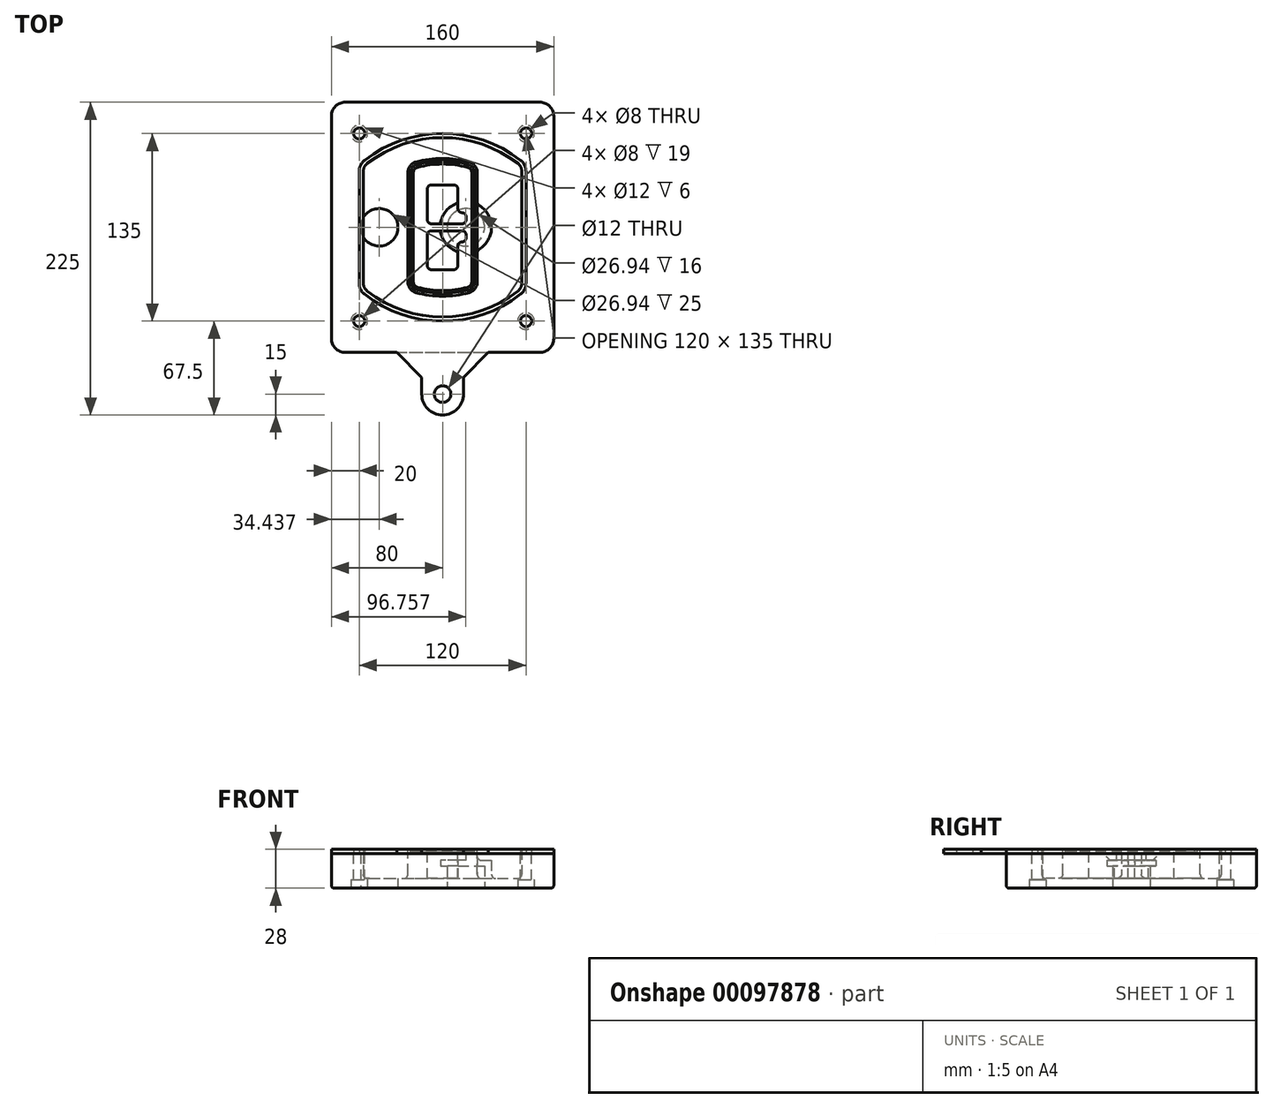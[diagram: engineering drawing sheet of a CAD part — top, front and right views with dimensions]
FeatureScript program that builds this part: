
annotation { "Feature Type Name" : "Feature", "Feature Type Description" : "" }
export const myFeature = defineFeature(function(context is Context, id is Id, definition is map)
    precondition{}
    {
        {
            var Q0;
            Q0=qCreatedBy(makeId("Top.planeOp"),FACE);
            var sketch = newSketch(context, id + "F0", { "sketchPlane" : qUnion([Q0])});
            skPoint(sketch, "E0.rect.middle", {"position": v(0, 0) * mm});
            skLineSegment(sketch, "E1.bottom", {"start": v(-70, -90) * mm, "end": v(70, -90) * mm});
            skLineSegment(sketch, "E1.top", {"start": v(-70, 90) * mm, "end": v(70, 90) * mm});
            skLineSegment(sketch, "E1.left", {"start": v(-80, -80) * mm, "end": v(-80, 80) * mm});
            skLineSegment(sketch, "E1.right", {"start": v(80, -80) * mm, "end": v(80, 80) * mm});
            skLineSegment(sketch, "E2", {"start": v(-80, 90) * mm, "end": v(80, -90) * mm, "construction": true});
            skLineSegment(sketch, "E3", {"start": v(80, 90) * mm, "end": v(-80, -90) * mm, "construction": true});
            skCircle(sketch, "E4", {"center": v(-60, 67.5) * mm, "radius": 4 * mm});
            skCircle(sketch, "E5", {"center": v(60, 67.5) * mm, "radius": 4 * mm});
            skCircle(sketch, "E6", {"center": v(60, -67.5) * mm, "radius": 4 * mm});
            skCircle(sketch, "E7", {"center": v(-60, -67.5) * mm, "radius": 4 * mm});
            skLineSegment(sketch, "E8", {"start": v(-60, 67.5) * mm, "end": v(60, 67.5) * mm, "construction": true});
            skLineSegment(sketch, "E9", {"start": v(60, 67.5) * mm, "end": v(60, -67.5) * mm, "construction": true});
            skLineSegment(sketch, "E10", {"start": v(60, -67.5) * mm, "end": v(-60, -67.5) * mm, "construction": true});
            skLineSegment(sketch, "E11", {"start": v(-60, -67.5) * mm, "end": v(-60, 67.5) * mm, "construction": true});
            skLineSegment(sketch, "E12", {"start": v(-60, 40.3) * mm, "end": v(-60, -40.3) * mm});
            skLineSegment(sketch, "E13", {"start": v(60, 40.3) * mm, "end": v(60, -40.3) * mm});
            skArc(sketch, "E14", {"start": v(56.15, 48.18) * mm, "mid": v(0, 67.5) * mm, "end": v(-56.15, 48.18) * mm});
            skArc(sketch, "E15", {"start": v(-56.15, -48.18) * mm, "mid": v(0, -67.5) * mm, "end": v(56.15, -48.18) * mm});
            skLineSegment(sketch, "E16", {"start": v(-60, 0) * mm, "end": v(60, 0) * mm, "construction": true});
            skPoint(sketch, "E17.visualSharp", {"position": v(-60, -45) * mm});
            skArc(sketch, "E17.filletArc", {"start": v(-60, -40.3) * mm, "mid": v(-58.99, -44.68) * mm, "end": v(-56.15, -48.18) * mm});
            skPoint(sketch, "E18.visualSharp", {"position": v(-60, 45) * mm});
            skArc(sketch, "E18.filletArc", {"start": v(-56.15, 48.18) * mm, "mid": v(-58.99, 44.68) * mm, "end": v(-60, 40.3) * mm});
            skPoint(sketch, "E19.visualSharp", {"position": v(60, 45) * mm});
            skArc(sketch, "E19.filletArc", {"start": v(60, 40.3) * mm, "mid": v(58.99, 44.68) * mm, "end": v(56.15, 48.18) * mm});
            skPoint(sketch, "E20.visualSharp", {"position": v(60, -45) * mm});
            skArc(sketch, "E20.filletArc", {"start": v(56.15, -48.18) * mm, "mid": v(58.99, -44.68) * mm, "end": v(60, -40.3) * mm});
            skPoint(sketch, "E21.visualSharp", {"position": v(-80, 90) * mm});
            skArc(sketch, "E21.filletArc", {"start": v(-70, 90) * mm, "mid": v(-77.07, 87.07) * mm, "end": v(-80, 80) * mm});
            skPoint(sketch, "E22.visualSharp", {"position": v(80, 90) * mm});
            skArc(sketch, "E22.filletArc", {"start": v(80, 80) * mm, "mid": v(77.07, 87.07) * mm, "end": v(70, 90) * mm});
            skPoint(sketch, "E23.visualSharp", {"position": v(80, -90) * mm});
            skArc(sketch, "E23.filletArc", {"start": v(70, -90) * mm, "mid": v(77.07, -87.07) * mm, "end": v(80, -80) * mm});
            skPoint(sketch, "E24.visualSharp", {"position": v(-80, -90) * mm});
            skArc(sketch, "E24.filletArc", {"start": v(-80, -80) * mm, "mid": v(-77.07, -87.07) * mm, "end": v(-70, -90) * mm});
            skArc(sketch, "E25.0", {"start": v(57, 40.3) * mm, "mid": v(56.3, 43.36) * mm, "end": v(54.3, 45.81) * mm});
            skLineSegment(sketch, "E25.1", {"start": v(57, 40.3) * mm, "end": v(57, -40.3) * mm});
            skArc(sketch, "E25.2", {"start": v(54.3, -45.81) * mm, "mid": v(56.3, -43.36) * mm, "end": v(57, -40.3) * mm});
            skArc(sketch, "E25.3", {"start": v(-54.3, -45.81) * mm, "mid": v(0, -64.5) * mm, "end": v(54.3, -45.81) * mm});
            skArc(sketch, "E25.4", {"start": v(-57, -40.3) * mm, "mid": v(-56.3, -43.36) * mm, "end": v(-54.3, -45.81) * mm});
            skArc(sketch, "E25.5", {"start": v(54.3, 45.81) * mm, "mid": v(0, 64.5) * mm, "end": v(-54.3, 45.81) * mm});
            skLineSegment(sketch, "E25.6", {"start": v(-57, 40.3) * mm, "end": v(-57, -40.3) * mm});
            skArc(sketch, "E25.7", {"start": v(-54.3, 45.81) * mm, "mid": v(-56.3, 43.36) * mm, "end": v(-57, 40.3) * mm});
            skArc(sketch, "E26.0", {"start": v(-58.62, 51.33) * mm, "mid": v(-62.58, 46.43) * mm, "end": v(-64, 40.3) * mm});
            skArc(sketch, "E26.1", {"start": v(58.62, 51.33) * mm, "mid": v(0, 71.5) * mm, "end": v(-58.62, 51.33) * mm});
            skArc(sketch, "E26.2", {"start": v(64, 40.3) * mm, "mid": v(62.58, 46.43) * mm, "end": v(58.62, 51.33) * mm});
            skLineSegment(sketch, "E26.3", {"start": v(64, 40.3) * mm, "end": v(64, -40.3) * mm});
            skArc(sketch, "E26.4", {"start": v(58.62, -51.33) * mm, "mid": v(62.58, -46.43) * mm, "end": v(64, -40.3) * mm});
            skLineSegment(sketch, "E26.5", {"start": v(-64, 40.3) * mm, "end": v(-64, -40.3) * mm});
            skArc(sketch, "E26.6", {"start": v(-58.62, -51.33) * mm, "mid": v(0, -71.5) * mm, "end": v(58.62, -51.33) * mm});
            skArc(sketch, "E26.7", {"start": v(-64, -40.3) * mm, "mid": v(-62.58, -46.43) * mm, "end": v(-58.62, -51.33) * mm});
            skSolve(sketch);
        }
        {
            var Q0;
            Q0=makeQuery(id+"F0.imprint","IMPRINT",FACE,{"disambiguationData":[TD([[makeQuery(id+"F0.imprint","IMPRINT",EDGE,{"derivedFrom":sQuery(id+"F0.wireOp",EDGE,"E1.bottom")}),1.0]])]});
            var Q1;
            Q1=makeQuery(id+"F0.imprint","IMPRINT",FACE,{"disambiguationData":[TD([[makeQuery(id+"F0.imprint","IMPRINT",EDGE,{"derivedFrom":sQuery(id+"F0.wireOp",EDGE,"E12")}),1.0]])]});
            var Q2;
            Q2=makeQuery(id+"F0.imprint","IMPRINT",FACE,{"disambiguationData":[TD([[makeQuery(id+"F0.imprint","IMPRINT",EDGE,{"derivedFrom":sQuery(id+"F0.wireOp",EDGE,"E25.0")}),1.0]])]});
            var Q3;
            Q3=makeQuery(id+"F0.imprint","IMPRINT",FACE,{"disambiguationData":[TD([[makeQuery(id+"F0.imprint","IMPRINT",EDGE,{"derivedFrom":sQuery(id+"F0.wireOp",EDGE,"E12")}),-1.0]])]});
            extrude(context, id + "F1", {"entities" : qUnion([Q0, Q1, Q2, Q3]), "oppositeDirection" : true, "depth" : 25 * mm});
        }
        {
            var Q0;
            Q0=makeQuery(id+"F0.imprint","IMPRINT",FACE,{"disambiguationData":[TD([[makeQuery(id+"F0.imprint","IMPRINT",EDGE,{"derivedFrom":sQuery(id+"F0.wireOp",EDGE,"E12")}),1.0]])]});
            extrude(context, id + "F2", {"entities" : qUnion([Q0]), "operationType" : NewBodyOperationType.ADD, "depth" : 3 * mm});
        }
        {
            var Q0;
            Q0=makeQuery(id+"F0.imprint","IMPRINT",FACE,{"disambiguationData":[TD([[makeQuery(id+"F0.imprint","IMPRINT",EDGE,{"derivedFrom":sQuery(id+"F0.wireOp",EDGE,"E25.0")}),1.0]])]});
            extrude(context, id + "F3", {"entities" : qUnion([Q0]), "operationType" : NewBodyOperationType.REMOVE, "oppositeDirection" : true, "depth" : 18 * mm});
        }
        {
            var Q0;
            Q0=makeQuery(id+"F2.opExtrude","CAP_FACE",FACE,{"disambiguationData":[OSD([sQuery(id+"F0.wireOp",EDGE,"E12"),sQuery(id+"F0.wireOp",EDGE,"E13"),sQuery(id+"F0.wireOp",EDGE,"E14"),sQuery(id+"F0.wireOp",EDGE,"E15"),sQuery(id+"F0.wireOp",EDGE,"E17.filletArc"),sQuery(id+"F0.wireOp",EDGE,"E18.filletArc"),sQuery(id+"F0.wireOp",EDGE,"E19.filletArc"),sQuery(id+"F0.wireOp",EDGE,"E20.filletArc"),sQuery(id+"F0.wireOp",EDGE,"E25.0"),sQuery(id+"F0.wireOp",EDGE,"E25.1"),sQuery(id+"F0.wireOp",EDGE,"E25.2"),sQuery(id+"F0.wireOp",EDGE,"E25.3"),sQuery(id+"F0.wireOp",EDGE,"E25.4"),sQuery(id+"F0.wireOp",EDGE,"E25.5"),sQuery(id+"F0.wireOp",EDGE,"E25.6"),sQuery(id+"F0.wireOp",EDGE,"E25.7")])],"isStart":false});
            var sketch = newSketch(context, id + "F4", { "sketchPlane" : qUnion([Q0])});
            skArc(sketch, "E27.0", {"start": v(-19.08, -46.97) * mm, "mid": v(0, -49.5) * mm, "end": v(19.08, -46.97) * mm});
            skArc(sketch, "E28.0", {"start": v(19.08, 46.97) * mm, "mid": v(0, 49.5) * mm, "end": v(-19.08, 46.97) * mm});
            skLineSegment(sketch, "E29", {"start": v(-25, 39.25) * mm, "end": v(-25, -39.25) * mm});
            skLineSegment(sketch, "E30", {"start": v(25, 39.25) * mm, "end": v(25, -39.25) * mm});
            skLineSegment(sketch, "E31", {"start": v(-25, 45.1) * mm, "end": v(25, 45.1) * mm, "construction": true});
            skLineSegment(sketch, "E32", {"start": v(-25, -45.1) * mm, "end": v(25, -45.1) * mm, "construction": true});
            skPoint(sketch, "E33.visualSharp", {"position": v(-25, 45.1) * mm});
            skArc(sketch, "E33.filletArc", {"start": v(-19.08, 46.97) * mm, "mid": v(-23.35, 44.11) * mm, "end": v(-25, 39.25) * mm});
            skPoint(sketch, "E34.visualSharp", {"position": v(25, 45.1) * mm});
            skArc(sketch, "E34.filletArc", {"start": v(25, 39.25) * mm, "mid": v(23.35, 44.11) * mm, "end": v(19.08, 46.97) * mm});
            skPoint(sketch, "E35.visualSharp", {"position": v(25, -45.1) * mm});
            skArc(sketch, "E35.filletArc", {"start": v(19.08, -46.97) * mm, "mid": v(23.35, -44.11) * mm, "end": v(25, -39.25) * mm});
            skPoint(sketch, "E36.visualSharp", {"position": v(-25, -45.1) * mm});
            skArc(sketch, "E36.filletArc", {"start": v(-25, -39.25) * mm, "mid": v(-23.35, -44.11) * mm, "end": v(-19.08, -46.97) * mm});
            skArc(sketch, "E37.0", {"start": v(54.3, 45.81) * mm, "mid": v(0, 64.5) * mm, "end": v(-54.3, 45.81) * mm});
            skArc(sketch, "E37.1", {"start": v(-54.3, 45.81) * mm, "mid": v(-56.3, 43.36) * mm, "end": v(-57, 40.3) * mm});
            skLineSegment(sketch, "E37.2", {"start": v(-57, 40.3) * mm, "end": v(-57, -40.3) * mm});
            skArc(sketch, "E37.3", {"start": v(-57, -40.3) * mm, "mid": v(-56.3, -43.36) * mm, "end": v(-54.3, -45.81) * mm});
            skArc(sketch, "E37.4", {"start": v(-54.3, -45.81) * mm, "mid": v(0, -64.5) * mm, "end": v(54.3, -45.81) * mm});
            skArc(sketch, "E37.5", {"start": v(54.3, -45.81) * mm, "mid": v(56.3, -43.36) * mm, "end": v(57, -40.3) * mm});
            skLineSegment(sketch, "E37.6", {"start": v(57, 40.3) * mm, "end": v(57, -40.3) * mm});
            skArc(sketch, "E37.7", {"start": v(57, 40.3) * mm, "mid": v(56.3, 43.36) * mm, "end": v(54.3, 45.81) * mm});
            skLineSegment(sketch, "E38.0", {"start": v(23, 39.25) * mm, "end": v(23, -39.25) * mm});
            skArc(sketch, "E38.1", {"start": v(18.56, -45.04) * mm, "mid": v(21.76, -42.9) * mm, "end": v(23, -39.25) * mm});
            skArc(sketch, "E38.2", {"start": v(-18.56, -45.04) * mm, "mid": v(0, -47.5) * mm, "end": v(18.56, -45.04) * mm});
            skArc(sketch, "E38.3", {"start": v(-23, -39.25) * mm, "mid": v(-21.76, -42.9) * mm, "end": v(-18.56, -45.04) * mm});
            skLineSegment(sketch, "E38.4", {"start": v(-23, 39.25) * mm, "end": v(-23, -39.25) * mm});
            skArc(sketch, "E38.5", {"start": v(23, 39.25) * mm, "mid": v(21.76, 42.9) * mm, "end": v(18.56, 45.04) * mm});
            skArc(sketch, "E38.6", {"start": v(-18.56, 45.04) * mm, "mid": v(-21.76, 42.9) * mm, "end": v(-23, 39.25) * mm});
            skArc(sketch, "E38.7", {"start": v(18.56, 45.04) * mm, "mid": v(0, 47.5) * mm, "end": v(-18.56, 45.04) * mm});
            skArc(sketch, "E39.0", {"start": v(21, 39.25) * mm, "mid": v(20.18, 41.68) * mm, "end": v(18.04, 43.1) * mm});
            skLineSegment(sketch, "E39.1", {"start": v(21, 39.25) * mm, "end": v(21, -39.25) * mm});
            skArc(sketch, "E39.2", {"start": v(18.04, -43.1) * mm, "mid": v(20.18, -41.68) * mm, "end": v(21, -39.25) * mm});
            skArc(sketch, "E39.3", {"start": v(-18.04, -43.1) * mm, "mid": v(0, -45.5) * mm, "end": v(18.04, -43.1) * mm});
            skArc(sketch, "E39.4", {"start": v(-21, -39.25) * mm, "mid": v(-20.18, -41.68) * mm, "end": v(-18.04, -43.1) * mm});
            skArc(sketch, "E39.5", {"start": v(18.04, 43.1) * mm, "mid": v(0, 45.5) * mm, "end": v(-18.04, 43.1) * mm});
            skLineSegment(sketch, "E39.6", {"start": v(-21, 39.25) * mm, "end": v(-21, -39.25) * mm});
            skArc(sketch, "E39.7", {"start": v(-18.04, 43.1) * mm, "mid": v(-20.18, 41.68) * mm, "end": v(-21, 39.25) * mm});
            skLineSegment(sketch, "E40", {"start": v(-25, 0) * mm, "end": v(25, 0) * mm, "construction": true});
            skLineSegment(sketch, "E41", {"start": v(-11, 5.5) * mm, "end": v(-11, 27.5) * mm});
            skLineSegment(sketch, "E42", {"start": v(-8, 30.5) * mm, "end": v(8, 30.5) * mm});
            skLineSegment(sketch, "E43", {"start": v(11, 27.5) * mm, "end": v(11, 13.5) * mm});
            skLineSegment(sketch, "E44", {"start": v(14, 10.5) * mm, "end": v(14, 10.5) * mm});
            skLineSegment(sketch, "E45", {"start": v(17, 7.5) * mm, "end": v(17, 5.5) * mm});
            skLineSegment(sketch, "E46", {"start": v(14, 2.5) * mm, "end": v(-8, 2.5) * mm});
            skPoint(sketch, "E47.visualSharp", {"position": v(-11, 30.5) * mm});
            skArc(sketch, "E47.filletArc", {"start": v(-8, 30.5) * mm, "mid": v(-10.12, 29.62) * mm, "end": v(-11, 27.5) * mm});
            skPoint(sketch, "E48.visualSharp", {"position": v(11, 30.5) * mm});
            skArc(sketch, "E48.filletArc", {"start": v(11, 27.5) * mm, "mid": v(10.12, 29.62) * mm, "end": v(8, 30.5) * mm});
            skPoint(sketch, "E49.visualSharp", {"position": v(11, 10.5) * mm});
            skArc(sketch, "E49.filletArc", {"start": v(11, 13.5) * mm, "mid": v(11.88, 11.38) * mm, "end": v(14, 10.5) * mm});
            skPoint(sketch, "E50.visualSharp", {"position": v(17, 10.5) * mm});
            skArc(sketch, "E50.filletArc", {"start": v(17, 7.5) * mm, "mid": v(16.12, 9.62) * mm, "end": v(14, 10.5) * mm});
            skPoint(sketch, "E51.visualSharp", {"position": v(17, 2.5) * mm});
            skArc(sketch, "E51.filletArc", {"start": v(14, 2.5) * mm, "mid": v(16.12, 3.38) * mm, "end": v(17, 5.5) * mm});
            skPoint(sketch, "E52.visualSharp", {"position": v(-11, 2.5) * mm});
            skArc(sketch, "E52.filletArc", {"start": v(-11, 5.5) * mm, "mid": v(-10.12, 3.38) * mm, "end": v(-8, 2.5) * mm});
            skLineSegment(sketch, "E53.0.MirrorCS", {"start": v(14, -2.5) * mm, "end": v(-8, -2.5) * mm});
            skArc(sketch, "E54.0.MirrorCS", {"start": v(-11, -5.5) * mm, "mid": v(-10.12, -3.38) * mm, "end": v(-8, -2.5) * mm});
            skLineSegment(sketch, "E55.0.MirrorCS", {"start": v(-11, -5.5) * mm, "end": v(-11, -27.5) * mm});
            skArc(sketch, "E56.0.MirrorCS", {"start": v(-8, -30.5) * mm, "mid": v(-10.12, -29.62) * mm, "end": v(-11, -27.5) * mm});
            skLineSegment(sketch, "E57.0.MirrorCS", {"start": v(-8, -30.5) * mm, "end": v(8, -30.5) * mm});
            skArc(sketch, "E58.0.MirrorCS", {"start": v(11, -27.5) * mm, "mid": v(10.12, -29.62) * mm, "end": v(8, -30.5) * mm});
            skLineSegment(sketch, "E59.0.MirrorCS", {"start": v(11, -27.5) * mm, "end": v(11, -13.5) * mm});
            skArc(sketch, "E60.0.MirrorCS", {"start": v(11, -13.5) * mm, "mid": v(11.88, -11.38) * mm, "end": v(14, -10.5) * mm});
            skArc(sketch, "E61.0.MirrorCS", {"start": v(17, -7.5) * mm, "mid": v(16.12, -9.62) * mm, "end": v(14, -10.5) * mm});
            skLineSegment(sketch, "E62.0.MirrorCS", {"start": v(17, -7.5) * mm, "end": v(17, -5.5) * mm});
            skArc(sketch, "E63.0.MirrorCS", {"start": v(14, -2.5) * mm, "mid": v(16.12, -3.38) * mm, "end": v(17, -5.5) * mm});
            skSolve(sketch);
        }
        {
            var Q0;
            Q0=makeQuery(id+"F4.imprint","IMPRINT",FACE,{"disambiguationData":[TD([[makeQuery(id+"F4.imprint","IMPRINT",EDGE,{"derivedFrom":sQuery(id+"F4.wireOp",EDGE,"E27.0")}),1.0]])]});
            var Q1;
            Q1=makeQuery(id+"F4.imprint","IMPRINT",FACE,{"disambiguationData":[TD([[makeQuery(id+"F4.imprint","IMPRINT",EDGE,{"derivedFrom":sQuery(id+"F4.wireOp",EDGE,"E38.0")}),-1.0]])]});
            var Q2;
            Q2=makeQuery(id+"F4.imprint","IMPRINT",FACE,{"disambiguationData":[TD([[makeQuery(id+"F4.imprint","IMPRINT",EDGE,{"derivedFrom":sQuery(id+"F4.wireOp",EDGE,"E39.0")}),1.0]])]});
            extrude(context, id + "F5", {"entities" : qUnion([Q0, Q1, Q2]), "operationType" : NewBodyOperationType.ADD, "endBound" : BoundingType.UP_TO_NEXT, "oppositeDirection" : true, "depth" : 25 * mm});
        }
        {
            var Q0;
            Q0=makeQuery(id+"F4.imprint","IMPRINT",FACE,{"disambiguationData":[TD([[makeQuery(id+"F4.imprint","IMPRINT",EDGE,{"derivedFrom":sQuery(id+"F4.wireOp",EDGE,"E38.0")}),-1.0]])]});
            extrude(context, id + "F6", {"entities" : qUnion([Q0]), "operationType" : NewBodyOperationType.REMOVE, "oppositeDirection" : true, "depth" : 2 * mm});
        }
        {
            var Q0;
            Q0=makeQuery(id+"F1.opExtrude","CAP_FACE",FACE,{"disambiguationData":[OSD([sQuery(id+"F0.wireOp",EDGE,"E1.bottom"),sQuery(id+"F0.wireOp",EDGE,"E1.top"),sQuery(id+"F0.wireOp",EDGE,"E1.left"),sQuery(id+"F0.wireOp",EDGE,"E1.right"),sQuery(id+"F0.wireOp",EDGE,"E4"),sQuery(id+"F0.wireOp",EDGE,"E5"),sQuery(id+"F0.wireOp",EDGE,"E6"),sQuery(id+"F0.wireOp",EDGE,"E7"),sQuery(id+"F0.wireOp",EDGE,"E21.filletArc"),sQuery(id+"F0.wireOp",EDGE,"E22.filletArc"),sQuery(id+"F0.wireOp",EDGE,"E23.filletArc"),sQuery(id+"F0.wireOp",EDGE,"E24.filletArc")])],"isStart":false});
            var sketch = newSketch(context, id + "F7", { "sketchPlane" : qUnion([Q0])});
            skCircle(sketch, "E64", {"center": v(16.76, 0) * mm, "radius": 13.47 * mm});
            skCircle(sketch, "E65", {"center": v(-45.56, 0) * mm, "radius": 13.47 * mm});
            skLineSegment(sketch, "E66", {"start": v(80, 0) * mm, "end": v(-80, 0) * mm});
            skCircle(sketch, "E67", {"center": v(16.76, 0) * mm, "radius": 18.47 * mm});
            skCircle(sketch, "E68", {"center": v(60, -67.5) * mm, "radius": 6 * mm});
            skCircle(sketch, "E69", {"center": v(-60, -67.5) * mm, "radius": 6 * mm});
            skCircle(sketch, "E70", {"center": v(-60, 67.5) * mm, "radius": 6 * mm});
            skCircle(sketch, "E71", {"center": v(60, 67.5) * mm, "radius": 6 * mm});
            skSolve(sketch);
        }
        {
            var Q0;
            {var subQ1=sQuery(id+"F7.wireOp",EDGE,"E66");var subQ4=sQuery(id+"F7.wireOp",EDGE,"E64");var subQ6=makeQuery(id+"F7.imprint","INTERSECT",VERTEX,{"disambiguationData":[OD(0.0)],"derivedFrom":[subQ4,subQ1]});Q0=makeQuery(id+"F7.imprint","IMPRINT",FACE,{"disambiguationData":[TD([[makeQuery(id+"F7.imprint","IMPRINT",EDGE,{"disambiguationData":[TD([[subQ6,-1.0]])],"derivedFrom":subQ4}),-1.0]])]});}
            var Q1;
            {var subQ0=sQuery(id+"F7.wireOp",EDGE,"E66");var subQ1=sQuery(id+"F7.wireOp",EDGE,"E64");var subQ3=makeQuery(id+"F7.imprint","INTERSECT",VERTEX,{"disambiguationData":[OD(0.0)],"derivedFrom":[subQ1,subQ0]});Q1=makeQuery(id+"F7.imprint","IMPRINT",FACE,{"disambiguationData":[TD([[makeQuery(id+"F7.imprint","IMPRINT",EDGE,{"disambiguationData":[TD([[subQ3,-1.0]])],"derivedFrom":subQ1}),1.0]])]});}
            var Q2;
            {var subQ0=sQuery(id+"F7.wireOp",EDGE,"E66");var subQ1=sQuery(id+"F7.wireOp",EDGE,"E64");var subQ3=makeQuery(id+"F7.imprint","INTERSECT",VERTEX,{"disambiguationData":[OD(0.0)],"derivedFrom":[subQ1,subQ0]});Q2=makeQuery(id+"F7.imprint","IMPRINT",FACE,{"disambiguationData":[TD([[makeQuery(id+"F7.imprint","IMPRINT",EDGE,{"disambiguationData":[TD([[subQ3,1.0]])],"derivedFrom":subQ1}),1.0]])]});}
            var Q3;
            {var subQ1=sQuery(id+"F7.wireOp",EDGE,"E66");var subQ4=sQuery(id+"F7.wireOp",EDGE,"E64");var subQ6=makeQuery(id+"F7.imprint","INTERSECT",VERTEX,{"disambiguationData":[OD(0.0)],"derivedFrom":[subQ4,subQ1]});Q3=makeQuery(id+"F7.imprint","IMPRINT",FACE,{"disambiguationData":[TD([[makeQuery(id+"F7.imprint","IMPRINT",EDGE,{"disambiguationData":[TD([[subQ6,1.0]])],"derivedFrom":subQ4}),-1.0]])]});}
            extrude(context, id + "F8", {"entities" : qUnion([Q0, Q1, Q2, Q3]), "operationType" : NewBodyOperationType.ADD, "oppositeDirection" : true, "depth" : 20 * mm});
        }
        {
            var Q0;
            {var subQ0=sQuery(id+"F7.wireOp",EDGE,"E66");var subQ1=sQuery(id+"F7.wireOp",EDGE,"E64");var subQ3=makeQuery(id+"F7.imprint","INTERSECT",VERTEX,{"disambiguationData":[OD(0.0)],"derivedFrom":[subQ1,subQ0]});Q0=makeQuery(id+"F7.imprint","IMPRINT",FACE,{"disambiguationData":[TD([[makeQuery(id+"F7.imprint","IMPRINT",EDGE,{"disambiguationData":[TD([[subQ3,-1.0]])],"derivedFrom":subQ1}),1.0]])]});}
            var Q1;
            {var subQ0=sQuery(id+"F7.wireOp",EDGE,"E66");var subQ1=sQuery(id+"F7.wireOp",EDGE,"E64");var subQ3=makeQuery(id+"F7.imprint","INTERSECT",VERTEX,{"disambiguationData":[OD(0.0)],"derivedFrom":[subQ1,subQ0]});Q1=makeQuery(id+"F7.imprint","IMPRINT",FACE,{"disambiguationData":[TD([[makeQuery(id+"F7.imprint","IMPRINT",EDGE,{"disambiguationData":[TD([[subQ3,1.0]])],"derivedFrom":subQ1}),1.0]])]});}
            extrude(context, id + "F9", {"entities" : qUnion([Q0, Q1]), "operationType" : NewBodyOperationType.REMOVE, "oppositeDirection" : true, "depth" : 16 * mm});
        }
        {
            var Q0;
            {var subQ0=sQuery(id+"F7.wireOp",EDGE,"E66");var subQ1=sQuery(id+"F7.wireOp",EDGE,"E65");var subQ3=makeQuery(id+"F7.imprint","INTERSECT",VERTEX,{"disambiguationData":[OD(0.0)],"derivedFrom":[subQ1,subQ0]});Q0=makeQuery(id+"F7.imprint","IMPRINT",FACE,{"disambiguationData":[TD([[makeQuery(id+"F7.imprint","IMPRINT",EDGE,{"disambiguationData":[TD([[subQ3,-1.0]])],"derivedFrom":subQ1}),1.0]])]});}
            var Q1;
            {var subQ0=sQuery(id+"F7.wireOp",EDGE,"E66");var subQ1=sQuery(id+"F7.wireOp",EDGE,"E65");var subQ3=makeQuery(id+"F7.imprint","INTERSECT",VERTEX,{"disambiguationData":[OD(0.0)],"derivedFrom":[subQ1,subQ0]});Q1=makeQuery(id+"F7.imprint","IMPRINT",FACE,{"disambiguationData":[TD([[makeQuery(id+"F7.imprint","IMPRINT",EDGE,{"disambiguationData":[TD([[subQ3,1.0]])],"derivedFrom":subQ1}),1.0]])]});}
            extrude(context, id + "F10", {"entities" : qUnion([Q0, Q1]), "operationType" : NewBodyOperationType.REMOVE, "oppositeDirection" : true, "depth" : 25 * mm});
        }
        {
            var Q0;
            Q0=makeQuery(id+"F7.imprint","IMPRINT",FACE,{"disambiguationData":[TD([[makeQuery(id+"F7.imprint","IMPRINT",EDGE,{"derivedFrom":sQuery(id+"F7.wireOp",EDGE,"E68")}),1.0]])]});
            var Q1;
            Q1=makeQuery(id+"F7.imprint","IMPRINT",FACE,{"disambiguationData":[TD([[makeQuery(id+"F7.imprint","IMPRINT",EDGE,{"derivedFrom":makeQuery(id+"F1.opExtrude","CAP_EDGE",EDGE,{"disambiguationData":[OSD([sQuery(id+"F0.wireOp",EDGE,"E5")])],"isStart":false})}),-1.0]])]});
            var Q2;
            Q2=makeQuery(id+"F7.imprint","IMPRINT",FACE,{"disambiguationData":[TD([[makeQuery(id+"F7.imprint","IMPRINT",EDGE,{"derivedFrom":sQuery(id+"F7.wireOp",EDGE,"E69")}),1.0]])]});
            var Q3;
            Q3=makeQuery(id+"F7.imprint","IMPRINT",FACE,{"disambiguationData":[TD([[makeQuery(id+"F7.imprint","IMPRINT",EDGE,{"derivedFrom":makeQuery(id+"F1.opExtrude","CAP_EDGE",EDGE,{"disambiguationData":[OSD([sQuery(id+"F0.wireOp",EDGE,"E4")])],"isStart":false})}),-1.0]])]});
            var Q4;
            Q4=makeQuery(id+"F7.imprint","IMPRINT",FACE,{"disambiguationData":[TD([[makeQuery(id+"F7.imprint","IMPRINT",EDGE,{"derivedFrom":sQuery(id+"F7.wireOp",EDGE,"E70")}),1.0]])]});
            var Q5;
            Q5=makeQuery(id+"F7.imprint","IMPRINT",FACE,{"disambiguationData":[TD([[makeQuery(id+"F7.imprint","IMPRINT",EDGE,{"derivedFrom":makeQuery(id+"F1.opExtrude","CAP_EDGE",EDGE,{"disambiguationData":[OSD([sQuery(id+"F0.wireOp",EDGE,"E7")])],"isStart":false})}),-1.0]])]});
            var Q6;
            Q6=makeQuery(id+"F7.imprint","IMPRINT",FACE,{"disambiguationData":[TD([[makeQuery(id+"F7.imprint","IMPRINT",EDGE,{"derivedFrom":sQuery(id+"F7.wireOp",EDGE,"E71")}),1.0]])]});
            var Q7;
            Q7=makeQuery(id+"F7.imprint","IMPRINT",FACE,{"disambiguationData":[TD([[makeQuery(id+"F7.imprint","IMPRINT",EDGE,{"derivedFrom":makeQuery(id+"F1.opExtrude","CAP_EDGE",EDGE,{"disambiguationData":[OSD([sQuery(id+"F0.wireOp",EDGE,"E6")])],"isStart":false})}),-1.0]])]});
            extrude(context, id + "F11", {"entities" : qUnion([Q0, Q1, Q2, Q3, Q4, Q5, Q6, Q7]), "operationType" : NewBodyOperationType.REMOVE, "oppositeDirection" : true, "depth" : 6 * mm});
        }
        {
            var Q0;
            Q0=makeQuery(id+"F9.boolean.opBoolean","COPY",FACE,{"derivedFrom":makeQuery(id+"F9.opExtrude","CAP_FACE",FACE,{"disambiguationData":[OSD([sQuery(id+"F7.wireOp",EDGE,"E64")])],"isStart":false})});
            var sketch = newSketch(context, id + "F12", { "sketchPlane" : qUnion([Q0])});
            skArc(sketch, "E72.0", {"start": v(11, 17.55) * mm, "mid": v(2.57, 11.82) * mm, "end": v(-1.54, 2.5) * mm});
            skArc(sketch, "E72.1", {"start": v(-1.54, -2.5) * mm, "mid": v(2.57, -11.82) * mm, "end": v(11, -17.55) * mm});
            skLineSegment(sketch, "E73", {"start": v(-1.54, -2.5) * mm, "end": v(14, -2.5) * mm});
            skLineSegment(sketch, "E74.0", {"start": v(14, 2.5) * mm, "end": v(-1.54, 2.5) * mm});
            skArc(sketch, "E74.1", {"start": v(14, 2.5) * mm, "mid": v(16.12, 3.38) * mm, "end": v(17, 5.5) * mm});
            skLineSegment(sketch, "E74.2", {"start": v(17, 7.5) * mm, "end": v(17, 5.5) * mm});
            skArc(sketch, "E74.3", {"start": v(17, 7.5) * mm, "mid": v(16.12, 9.62) * mm, "end": v(14, 10.5) * mm});
            skArc(sketch, "E74.4", {"start": v(11, 13.5) * mm, "mid": v(11.88, 11.38) * mm, "end": v(14, 10.5) * mm});
            skLineSegment(sketch, "E74.5", {"start": v(11, 17.55) * mm, "end": v(11, 13.5) * mm});
            skLineSegment(sketch, "E74.7", {"start": v(14, -2.5) * mm, "end": v(-1.54, -2.5) * mm});
            skArc(sketch, "E74.8", {"start": v(14, -2.5) * mm, "mid": v(16.12, -3.38) * mm, "end": v(17, -5.5) * mm});
            skLineSegment(sketch, "E74.9", {"start": v(17, -7.5) * mm, "end": v(17, -5.5) * mm});
            skArc(sketch, "E74.10", {"start": v(17, -7.5) * mm, "mid": v(16.12, -9.62) * mm, "end": v(14, -10.5) * mm});
            skArc(sketch, "E74.11", {"start": v(11, -13.5) * mm, "mid": v(11.88, -11.38) * mm, "end": v(14, -10.5) * mm});
            skLineSegment(sketch, "E74.12", {"start": v(11, -17.55) * mm, "end": v(11, -13.5) * mm});
            skPoint(sketch, "E75.orphan", {"position": v(11, -27.5) * mm});
            skPoint(sketch, "E76.orphan", {"position": v(-8, -2.5) * mm});
            skPoint(sketch, "E77.orphan", {"position": v(-8, 2.5) * mm});
            skPoint(sketch, "E78.orphan", {"position": v(11, 27.5) * mm});
            skSolve(sketch);
        }
        {
            var Q0;
            {var subQ7=sQuery(id+"F12.wireOp",EDGE,"E72.0");var subQ14=sQuery(id+"F12.wireOp",EDGE,"E72.1");var subQ16=sQuery(id+"F12.wireOp",EDGE,"E74.1");var subQ18=sQuery(id+"F12.wireOp",EDGE,"E74.8");Q0=qUnion([makeQuery(id+"F12.imprint","IMPRINT",FACE,{"disambiguationData":[TD([[makeQuery(id+"F12.imprint","IMPRINT",EDGE,{"derivedFrom":subQ7}),1.0]])]}),makeQuery(id+"F12.imprint","IMPRINT",FACE,{"disambiguationData":[TD([[makeQuery(id+"F12.imprint","IMPRINT",EDGE,{"derivedFrom":subQ14}),1.0]])]}),makeQuery(id+"F12.imprint","IMPRINT",FACE,{"disambiguationData":[TD([[makeQuery(id+"F12.imprint","IMPRINT",EDGE,{"derivedFrom":subQ16}),1.0]])]}),makeQuery(id+"F12.imprint","IMPRINT",FACE,{"disambiguationData":[TD([[makeQuery(id+"F12.imprint","IMPRINT",EDGE,{"derivedFrom":subQ18}),-1.0]])]})]);}
            var Q1;
            Q1=makeQuery(id+"F5.boolean.opBoolean","SPLIT",FACE,{"disambiguationData":[TD([makeQuery(id+"F5.opExtrude","SWEPT_FACE",FACE,{"disambiguationData":[OSD([sQuery(id+"F4.wireOp",EDGE,"E41")])]})])],"derivedFrom":makeQuery(id+"F3.boolean.opBoolean","COPY",FACE,{"derivedFrom":makeQuery(id+"F3.opExtrude","CAP_FACE",FACE,{"disambiguationData":[OSD([sQuery(id+"F0.wireOp",EDGE,"E25.0"),sQuery(id+"F0.wireOp",EDGE,"E25.1"),sQuery(id+"F0.wireOp",EDGE,"E25.2"),sQuery(id+"F0.wireOp",EDGE,"E25.3"),sQuery(id+"F0.wireOp",EDGE,"E25.4"),sQuery(id+"F0.wireOp",EDGE,"E25.5"),sQuery(id+"F0.wireOp",EDGE,"E25.6"),sQuery(id+"F0.wireOp",EDGE,"E25.7")])],"isStart":false})})});
            extrude(context, id + "F13", {"entities" : qUnion([Q0]), "operationType" : NewBodyOperationType.REMOVE, "endBound" : BoundingType.UP_TO_SURFACE, "endBoundEntityFace" : qUnion([Q1]), "depth" : 25 * mm});
        }
        {
            var Q0;
            Q0=makeQuery(id+"F3.boolean.opBoolean","COPY",EDGE,{"derivedFrom":makeQuery(id+"F3.opExtrude","CAP_EDGE",EDGE,{"disambiguationData":[OSD([sQuery(id+"F0.wireOp",EDGE,"E25.6")])],"isStart":false})});
            var Q1;
            Q1=makeQuery(id+"F8.boolean.opBoolean","INTERSECT",EDGE,{"derivedFrom":[makeQuery(id+"F5.opExtrude","SWEPT_FACE",FACE,{"disambiguationData":[OSD([sQuery(id+"F4.wireOp",EDGE,"E30")])]}),makeQuery(id+"F8.opExtrude","CAP_FACE",FACE,{"disambiguationData":[OSD([sQuery(id+"F7.wireOp",EDGE,"E67")])],"isStart":false})]});
            var Q2;
            Q2=makeQuery(id+"F8.boolean.opBoolean","INTERSECT",EDGE,{"disambiguationData":[OD(1.0)],"derivedFrom":[makeQuery(id+"F5.opExtrude","SWEPT_FACE",FACE,{"disambiguationData":[OSD([sQuery(id+"F4.wireOp",EDGE,"E30")])]}),makeQuery(id+"F8.opExtrude","SWEPT_FACE",FACE,{"disambiguationData":[OSD([sQuery(id+"F7.wireOp",EDGE,"E67")])]})]});
            var Q3;
            {var subQ0=sQuery(id+"F4.wireOp",EDGE,"E30");Q3=makeQuery(id+"F8.boolean.opBoolean","SPLIT",EDGE,{"disambiguationData":[TD([makeQuery(id+"F5.opExtrude","SWEPT_FACE",FACE,{"disambiguationData":[OSD([sQuery(id+"F4.wireOp",EDGE,"E35.filletArc")])]})])],"derivedFrom":makeQuery(id+"F5.opExtrude","CAP_EDGE",EDGE,{"disambiguationData":[OSD([subQ0])],"isStart":false})});}
            var Q4;
            {var subQ0=sQuery(id+"F0.wireOp",EDGE,"E25.7");var subQ1=sQuery(id+"F0.wireOp",EDGE,"E25.1");var subQ2=sQuery(id+"F0.wireOp",EDGE,"E25.6");var subQ3=sQuery(id+"F0.wireOp",EDGE,"E25.5");var subQ4=sQuery(id+"F0.wireOp",EDGE,"E25.4");var subQ5=sQuery(id+"F0.wireOp",EDGE,"E25.0");var subQ6=sQuery(id+"F0.wireOp",EDGE,"E25.2");var subQ7=sQuery(id+"F0.wireOp",EDGE,"E25.3");Q4=makeQuery(id+"F8.boolean.opBoolean","INTERSECT",EDGE,{"derivedFrom":[makeQuery(id+"F5.boolean.opBoolean","SPLIT",FACE,{"disambiguationData":[TD([makeQuery(id+"F2.opExtrude","SWEPT_FACE",FACE,{"disambiguationData":[OSD([subQ5])]})])],"derivedFrom":makeQuery(id+"F3.boolean.opBoolean","COPY",FACE,{"derivedFrom":makeQuery(id+"F3.opExtrude","CAP_FACE",FACE,{"disambiguationData":[OSD([subQ5,subQ1,subQ6,subQ7,subQ4,subQ3,subQ2,subQ0])],"isStart":false})})}),makeQuery(id+"F8.opExtrude","SWEPT_FACE",FACE,{"disambiguationData":[OSD([sQuery(id+"F7.wireOp",EDGE,"E67")])]})]});}
            var Q5;
            Q5=makeQuery(id+"F8.boolean.opBoolean","INTERSECT",EDGE,{"disambiguationData":[OD(0.0)],"derivedFrom":[makeQuery(id+"F5.opExtrude","SWEPT_FACE",FACE,{"disambiguationData":[OSD([sQuery(id+"F4.wireOp",EDGE,"E30")])]}),makeQuery(id+"F8.opExtrude","SWEPT_FACE",FACE,{"disambiguationData":[OSD([sQuery(id+"F7.wireOp",EDGE,"E67")])]})]});
            fillet(context, id + "F14", {"entities" : qUnion([Q0, Q1, Q2, Q3, Q4, Q5]), "radius" : 3 * mm, "tangentPropagation" : true, "allowEdgeOverflow" : false});
        }
        {
            var Q0;
            Q0=makeQuery(id+"F1.opExtrude","CAP_EDGE",EDGE,{"disambiguationData":[OSD([sQuery(id+"F0.wireOp",EDGE,"E1.bottom")])],"isStart":false});
            fillet(context, id + "F15", {"entities" : qUnion([Q0]), "radius" : 2 * mm, "tangentPropagation" : true, "allowEdgeOverflow" : false});
        }
        {
            var Q0;
            {var subQ0=sQuery(id+"F0.wireOp",EDGE,"E22.filletArc");var subQ1=sQuery(id+"F0.wireOp",EDGE,"E7");var subQ2=sQuery(id+"F0.wireOp",EDGE,"E6");var subQ3=sQuery(id+"F0.wireOp",EDGE,"E5");var subQ4=sQuery(id+"F0.wireOp",EDGE,"E4");var subQ5=sQuery(id+"F0.wireOp",EDGE,"E1.bottom");var subQ6=sQuery(id+"F0.wireOp",EDGE,"E21.filletArc");var subQ7=sQuery(id+"F0.wireOp",EDGE,"E1.top");var subQ8=sQuery(id+"F0.wireOp",EDGE,"E1.left");var subQ9=sQuery(id+"F0.wireOp",EDGE,"E1.right");var subQ10=sQuery(id+"F0.wireOp",EDGE,"E23.filletArc");var subQ11=sQuery(id+"F0.wireOp",EDGE,"E24.filletArc");Q0=makeQuery(id+"F2.boolean.opBoolean","SPLIT",FACE,{"disambiguationData":[TD([makeQuery(id+"F1.opExtrude","SWEPT_FACE",FACE,{"disambiguationData":[OSD([subQ5])]})])],"derivedFrom":makeQuery(id+"F1.opExtrude","CAP_FACE",FACE,{"disambiguationData":[OSD([subQ5,subQ7,subQ8,subQ9,subQ4,subQ3,subQ2,subQ1,subQ6,subQ0,subQ10,subQ11])],"isStart":true})});}
            var sketch = newSketch(context, id + "F16", { "sketchPlane" : qUnion([Q0])});
            skLineSegment(sketch, "E79", {"start": v(0, 120) * mm, "end": v(0, 90) * mm, "construction": true});
            skCircle(sketch, "E80", {"center": v(0, 120) * mm, "radius": 6 * mm});
            skLineSegment(sketch, "E81", {"start": v(-15, 108) * mm, "end": v(-33, 90) * mm});
            skLineSegment(sketch, "E82.MirrorCS", {"start": v(15, 108) * mm, "end": v(33, 90) * mm});
            skLineSegment(sketch, "E83", {"start": v(-15, 120) * mm, "end": v(-15, 108) * mm});
            skLineSegment(sketch, "E84", {"start": v(15, 120) * mm, "end": v(15, 108) * mm});
            skArc(sketch, "E85", {"start": v(15, 120) * mm, "mid": v(0, 135) * mm, "end": v(-15, 120) * mm});
            skLineSegment(sketch, "E86", {"start": v(-80, 0) * mm, "end": v(80, 0) * mm, "construction": true});
            skArc(sketch, "E87.MirrorCS", {"start": v(-15, 120) * mm, "mid": v(0, 135) * mm, "end": v(15, 120) * mm});
            skLineSegment(sketch, "E88.MirrorCS", {"start": v(80, 0) * mm, "end": v(-80, 0) * mm, "construction": true});
            skLineSegment(sketch, "E89.MirrorCS", {"start": v(-15, -108) * mm, "end": v(-33, -90) * mm});
            skLineSegment(sketch, "E90.MirrorCS", {"start": v(-15, -120) * mm, "end": v(-15, -108) * mm});
            skArc(sketch, "E91.MirrorCS", {"start": v(-15, -120) * mm, "mid": v(0, -135) * mm, "end": v(15, -120) * mm});
            skLineSegment(sketch, "E92.MirrorCS", {"start": v(15, -120) * mm, "end": v(15, -108) * mm});
            skLineSegment(sketch, "E93.MirrorCS", {"start": v(15, -108) * mm, "end": v(33, -90) * mm});
            skCircle(sketch, "E94.MirrorC", {"center": v(0, -120) * mm, "radius": 6 * mm});
            skLineSegment(sketch, "E95.MirrorCS", {"start": v(0, -120) * mm, "end": v(0, -90) * mm, "construction": true});
            skSolve(sketch);
        }
        {
            var Q0;
            Q0=makeQuery(id+"F16.imprint","IMPRINT",FACE,{"disambiguationData":[TD([[makeQuery(id+"F16.imprint","IMPRINT",EDGE,{"derivedFrom":makeQuery(id+"F1.opExtrude","CAP_EDGE",EDGE,{"disambiguationData":[OSD([sQuery(id+"F0.wireOp",EDGE,"E1.left")])],"isStart":true})}),-1.0]])]});
            var Q1;
            Q1=makeQuery(id+"F16.imprint","IMPRINT",FACE,{"disambiguationData":[TD([[makeQuery(id+"F16.imprint","IMPRINT",EDGE,{"derivedFrom":sQuery(id+"F16.wireOp",EDGE,"E80")}),1.0]])]});
            var Q2;
            {var subQ0=sQuery(id+"F16.wireOp",EDGE,"E89.MirrorCS");Q2=makeQuery(id+"F16.imprint","IMPRINT",FACE,{"disambiguationData":[TD([[makeQuery(id+"F16.imprint","IMPRINT",EDGE,{"derivedFrom":subQ0}),-1.0]])]});}
            var Q3;
            Q3=makeQuery(id+"F2.opExtrude","CAP_FACE",FACE,{"disambiguationData":[OSD([sQuery(id+"F0.wireOp",EDGE,"E12"),sQuery(id+"F0.wireOp",EDGE,"E13"),sQuery(id+"F0.wireOp",EDGE,"E14"),sQuery(id+"F0.wireOp",EDGE,"E15"),sQuery(id+"F0.wireOp",EDGE,"E17.filletArc"),sQuery(id+"F0.wireOp",EDGE,"E18.filletArc"),sQuery(id+"F0.wireOp",EDGE,"E19.filletArc"),sQuery(id+"F0.wireOp",EDGE,"E20.filletArc"),sQuery(id+"F0.wireOp",EDGE,"E25.0"),sQuery(id+"F0.wireOp",EDGE,"E25.1"),sQuery(id+"F0.wireOp",EDGE,"E25.2"),sQuery(id+"F0.wireOp",EDGE,"E25.3"),sQuery(id+"F0.wireOp",EDGE,"E25.4"),sQuery(id+"F0.wireOp",EDGE,"E25.5"),sQuery(id+"F0.wireOp",EDGE,"E25.6"),sQuery(id+"F0.wireOp",EDGE,"E25.7")])],"isStart":false});
            extrude(context, id + "F17", {"entities" : qUnion([Q0, Q1, Q2]), "endBound" : BoundingType.UP_TO_SURFACE, "endBoundEntityFace" : qUnion([Q3]), "depth" : 25 * mm});
        }
    });
